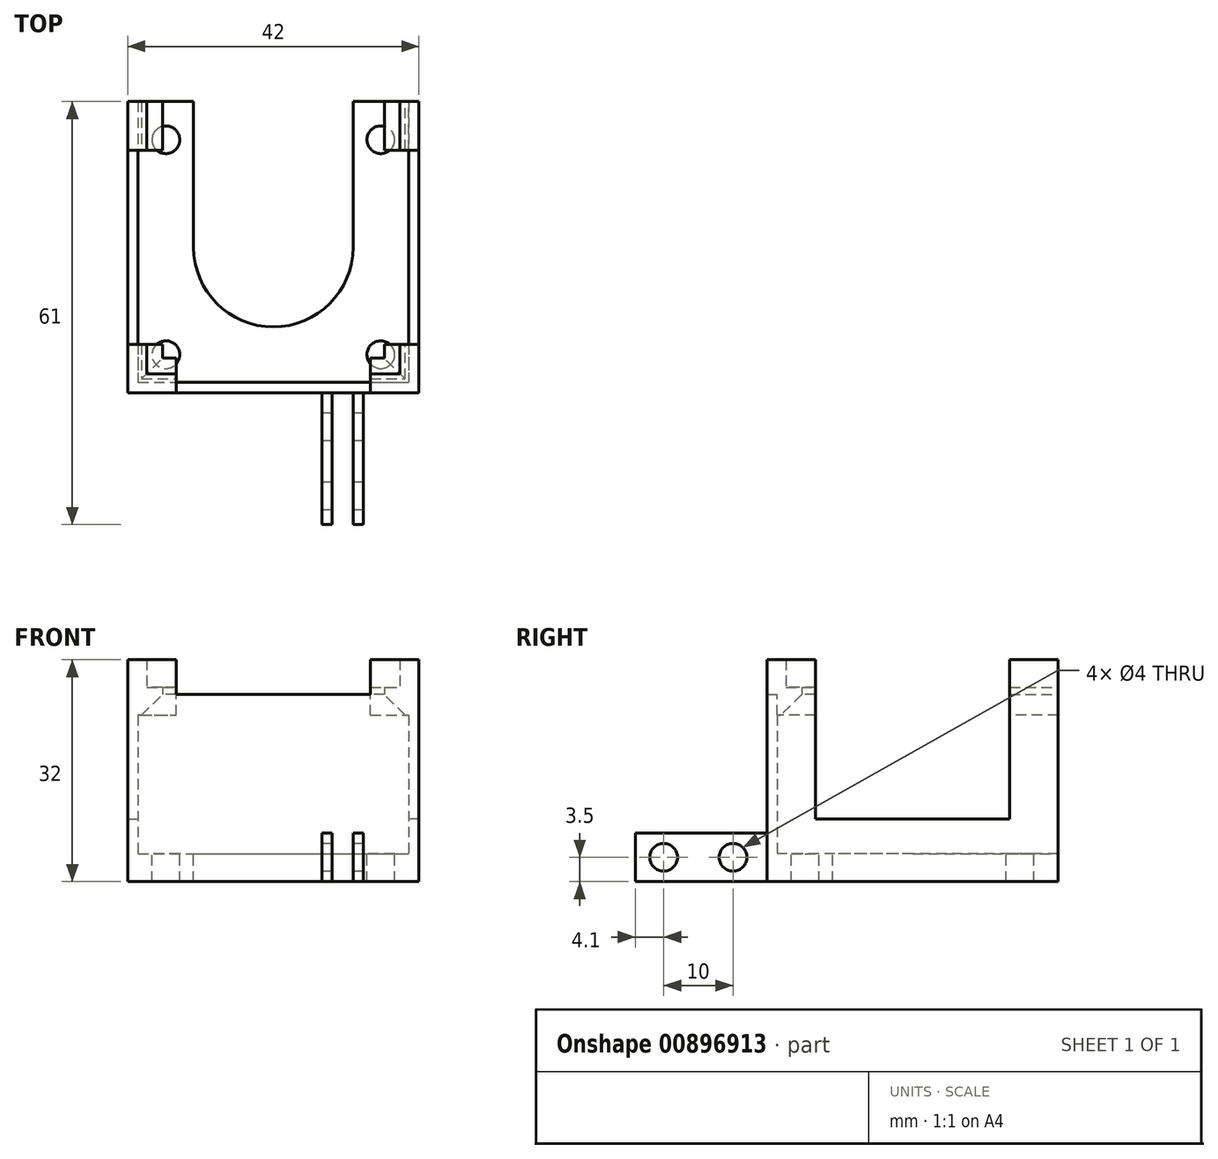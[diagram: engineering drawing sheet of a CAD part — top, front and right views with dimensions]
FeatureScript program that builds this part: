
annotation { "Feature Type Name" : "Feature", "Feature Type Description" : "" }
export const myFeature = defineFeature(function(context is Context, id is Id, definition is map)
    precondition{}
    {
        {
            var Q0;
            Q0=qCreatedBy(makeId("Top.planeOp"),FACE);
            var sketch = newSketch(context, id + "F0", { "sketchPlane" : qUnion([Q0])});
            skLineSegment(sketch, "E0.bottom", {"start": v(-19.5, 19.5) * mm, "end": v(19.5, 19.5) * mm});
            skLineSegment(sketch, "E0.top", {"start": v(-19.5, -19.5) * mm, "end": v(19.5, -19.5) * mm});
            skLineSegment(sketch, "E0.left", {"start": v(-19.5, 19.5) * mm, "end": v(-19.5, -19.5) * mm});
            skLineSegment(sketch, "E0.right", {"start": v(19.5, 19.5) * mm, "end": v(19.5, -19.5) * mm});
            skPoint(sketch, "E0.middle", {"position": v(0, 0) * mm});
            skLineSegment(sketch, "E1.0", {"start": v(21, 21) * mm, "end": v(21, -21) * mm});
            skLineSegment(sketch, "E1.1", {"start": v(-21, 21) * mm, "end": v(21, 21) * mm});
            skLineSegment(sketch, "E1.2", {"start": v(-21, 21) * mm, "end": v(-21, -21) * mm});
            skLineSegment(sketch, "E1.3", {"start": v(-21, -21) * mm, "end": v(21, -21) * mm});
            skLineSegment(sketch, "E2", {"start": v(21, 21) * mm, "end": v(21, 14) * mm});
            skLineSegment(sketch, "E3", {"start": v(21, 14) * mm, "end": v(19.5, 14) * mm});
            skLineSegment(sketch, "E4", {"start": v(-21, 14) * mm, "end": v(-19.5, 14) * mm});
            skLineSegment(sketch, "E5", {"start": v(-21, -14) * mm, "end": v(-19.5, -14) * mm});
            skLineSegment(sketch, "E6", {"start": v(-14, -19.5) * mm, "end": v(-14, -21) * mm});
            skLineSegment(sketch, "E7", {"start": v(14, -21) * mm, "end": v(14, -19.5) * mm});
            skLineSegment(sketch, "E8", {"start": v(21, -14) * mm, "end": v(19.5, -14) * mm});
            skLineSegment(sketch, "E9", {"start": v(-21, 14) * mm, "end": v(-21, 21) * mm});
            skCircle(sketch, "E10", {"center": v(0, 0) * mm, "radius": 11.5 * mm});
            skCircle(sketch, "E11", {"center": v(-15.5, 15.5) * mm, "radius": 2 * mm});
            skCircle(sketch, "E12", {"center": v(15.5, 15.5) * mm, "radius": 2 * mm});
            skCircle(sketch, "E13", {"center": v(15.5, -15.5) * mm, "radius": 2 * mm});
            skCircle(sketch, "E14", {"center": v(-15.5, -15.5) * mm, "radius": 2 * mm});
            skLineSegment(sketch, "E15", {"start": v(-19.5, 19.5) * mm, "end": v(-19.5, 21) * mm});
            skLineSegment(sketch, "E16", {"start": v(19.5, 19.5) * mm, "end": v(19.5, 21) * mm});
            skLineSegment(sketch, "E17", {"start": v(-21, -21) * mm, "end": v(-14, -21) * mm});
            skLineSegment(sketch, "E18", {"start": v(-11.5, 0) * mm, "end": v(-11.5, 21) * mm});
            skLineSegment(sketch, "E19", {"start": v(11.5, 0) * mm, "end": v(11.5, 21) * mm});
            skSolve(sketch);
        }
        {
            var Q0;
            Q0=makeQuery(id+"F0.imprint","IMPRINT",FACE,{"disambiguationData":[TD([[makeQuery(id+"F0.imprint","IMPRINT",EDGE,{"derivedFrom":sQuery(id+"F0.wireOp",EDGE,"E11")}),-1.0]])]});
            var Q1;
            {var subQ0=sQuery(id+"F0.wireOp",EDGE,"E4");Q1=makeQuery(id+"F0.imprint","IMPRINT",FACE,{"disambiguationData":[TD([[makeQuery(id+"F0.imprint","IMPRINT",EDGE,{"derivedFrom":subQ0}),-1.0]])]});}
            var Q2;
            {var subQ0=sQuery(id+"F0.wireOp",EDGE,"E3");Q2=makeQuery(id+"F0.imprint","IMPRINT",FACE,{"disambiguationData":[TD([[makeQuery(id+"F0.imprint","IMPRINT",EDGE,{"derivedFrom":subQ0}),-1.0]])]});}
            var Q3;
            {var subQ4=sQuery(id+"F0.wireOp",EDGE,"E7");Q3=makeQuery(id+"F0.imprint","IMPRINT",FACE,{"disambiguationData":[TD([[makeQuery(id+"F0.imprint","IMPRINT",EDGE,{"derivedFrom":subQ4}),-1.0]])]});}
            var Q4;
            {var subQ3=sQuery(id+"F0.wireOp",EDGE,"E5");Q4=makeQuery(id+"F0.imprint","IMPRINT",FACE,{"disambiguationData":[TD([[makeQuery(id+"F0.imprint","IMPRINT",EDGE,{"derivedFrom":subQ3}),-1.0]])]});}
            var Q5;
            {var subQ0=sQuery(id+"F0.wireOp",EDGE,"E4");Q5=makeQuery(id+"F0.imprint","IMPRINT",FACE,{"disambiguationData":[TD([[makeQuery(id+"F0.imprint","IMPRINT",EDGE,{"derivedFrom":subQ0}),1.0]])]});}
            var Q6;
            {var subQ0=sQuery(id+"F0.wireOp",EDGE,"E3");Q6=makeQuery(id+"F0.imprint","IMPRINT",FACE,{"disambiguationData":[TD([[makeQuery(id+"F0.imprint","IMPRINT",EDGE,{"derivedFrom":subQ0}),1.0]])]});}
            var Q7;
            {var subQ0=sQuery(id+"F0.wireOp",EDGE,"E6");Q7=makeQuery(id+"F0.imprint","IMPRINT",FACE,{"disambiguationData":[TD([[makeQuery(id+"F0.imprint","IMPRINT",EDGE,{"derivedFrom":subQ0}),1.0]])]});}
            var Q8;
            {var subQ3=sQuery(id+"F0.wireOp",EDGE,"E15");Q8=makeQuery(id+"F0.imprint","IMPRINT",FACE,{"disambiguationData":[TD([[makeQuery(id+"F0.imprint","IMPRINT",EDGE,{"derivedFrom":subQ3}),-1.0]])]});}
            var Q9;
            {var subQ0=sQuery(id+"F0.wireOp",EDGE,"E16");Q9=makeQuery(id+"F0.imprint","IMPRINT",FACE,{"disambiguationData":[TD([[makeQuery(id+"F0.imprint","IMPRINT",EDGE,{"derivedFrom":subQ0}),1.0]])]});}
            extrude(context, id + "F1", {"entities" : qUnion([Q0, Q1, Q2, Q3, Q4, Q5, Q6, Q7, Q8, Q9]), "oppositeDirection" : true, "depth" : 4 * mm, "offsetDistance" : 25 * mm});
        }
        {
            var Q0;
            {var subQ3=sQuery(id+"F0.wireOp",EDGE,"E5");Q0=makeQuery(id+"F0.imprint","IMPRINT",FACE,{"disambiguationData":[TD([[makeQuery(id+"F0.imprint","IMPRINT",EDGE,{"derivedFrom":subQ3}),-1.0]])]});}
            var Q1;
            {var subQ4=sQuery(id+"F0.wireOp",EDGE,"E7");Q1=makeQuery(id+"F0.imprint","IMPRINT",FACE,{"disambiguationData":[TD([[makeQuery(id+"F0.imprint","IMPRINT",EDGE,{"derivedFrom":subQ4}),-1.0]])]});}
            var Q2;
            Q2=makeQuery(id+"F0.imprint","IMPRINT",FACE,{"disambiguationData":[TD([[makeQuery(id+"F0.imprint","IMPRINT",EDGE,{"derivedFrom":sQuery(id+"F0.wireOp",EDGE,"wOJEcjxp-KVov-CLC1-gWga-9RxFXBWaR2St")}),-1.0]])]});
            var Q3;
            {var subQ0=sQuery(id+"F0.wireOp",EDGE,"y9VzjcNx-FhIy-98Bx-Yjvf-nXmHwvDM8nUN");Q3=makeQuery(id+"F0.imprint","IMPRINT",FACE,{"disambiguationData":[TD([[makeQuery(id+"F0.imprint","IMPRINT",EDGE,{"derivedFrom":subQ0}),1.0]])]});}
            var Q4;
            {var subQ0=sQuery(id+"F0.wireOp",EDGE,"E4");Q4=makeQuery(id+"F0.imprint","IMPRINT",FACE,{"disambiguationData":[TD([[makeQuery(id+"F0.imprint","IMPRINT",EDGE,{"derivedFrom":subQ0}),1.0]])]});}
            var Q5;
            {var subQ0=sQuery(id+"F0.wireOp",EDGE,"E3");Q5=makeQuery(id+"F0.imprint","IMPRINT",FACE,{"disambiguationData":[TD([[makeQuery(id+"F0.imprint","IMPRINT",EDGE,{"derivedFrom":subQ0}),-1.0]])]});}
            var Q6;
            {var subQ0=sQuery(id+"F0.wireOp",EDGE,"E6");Q6=makeQuery(id+"F0.imprint","IMPRINT",FACE,{"disambiguationData":[TD([[makeQuery(id+"F0.imprint","IMPRINT",EDGE,{"derivedFrom":subQ0}),1.0]])]});}
            extrude(context, id + "F2", {"entities" : qUnion([Q0, Q1, Q2, Q3, Q4, Q5, Q6]), "operationType" : NewBodyOperationType.ADD, "depth" : 23 * mm, "offsetDistance" : 25 * mm});
        }
        {
            var Q0;
            {var subQ0=sQuery(id+"F0.wireOp",EDGE,"E3");Q0=makeQuery(id+"F0.imprint","IMPRINT",FACE,{"disambiguationData":[TD([[makeQuery(id+"F0.imprint","IMPRINT",EDGE,{"derivedFrom":subQ0}),1.0]])]});}
            var Q1;
            {var subQ0=sQuery(id+"F0.wireOp",EDGE,"E4");Q1=makeQuery(id+"F0.imprint","IMPRINT",FACE,{"disambiguationData":[TD([[makeQuery(id+"F0.imprint","IMPRINT",EDGE,{"derivedFrom":subQ0}),-1.0]])]});}
            extrude(context, id + "F3", {"entities" : qUnion([Q0, Q1]), "operationType" : NewBodyOperationType.ADD, "depth" : 5 * mm, "offsetDistance" : 25 * mm});
        }
        {
            var Q0;
            Q0=makeQuery(id+"F2.opExtrude","CAP_FACE",FACE,{"disambiguationData":[OSD([sQuery(id+"F0.wireOp",EDGE,"E0.top"),sQuery(id+"F0.wireOp",EDGE,"E0.left"),sQuery(id+"F0.wireOp",EDGE,"E0.right"),sQuery(id+"F0.wireOp",EDGE,"E1.0"),sQuery(id+"F0.wireOp",EDGE,"E1.2"),sQuery(id+"F0.wireOp",EDGE,"E1.3"),sQuery(id+"F0.wireOp",EDGE,"E5"),sQuery(id+"F0.wireOp",EDGE,"E8")])],"isStart":false});
            var sketch = newSketch(context, id + "F4", { "sketchPlane" : qUnion([Q0])});
            skPoint(sketch, "E20", {"position": v(21, 21) * mm});
            skPoint(sketch, "E21", {"position": v(-21, 21) * mm});
            skPoint(sketch, "E22", {"position": v(21, -21) * mm});
            skPoint(sketch, "E23", {"position": v(-21, -21) * mm});
            skPoint(sketch, "E24", {"position": v(-21, 14) * mm});
            skPoint(sketch, "E25", {"position": v(21, 14) * mm});
            skPoint(sketch, "E26", {"position": v(21, -14) * mm});
            skPoint(sketch, "E27", {"position": v(14, -21) * mm});
            skPoint(sketch, "E28", {"position": v(-14, -21) * mm});
            skPoint(sketch, "E29", {"position": v(-21, -14) * mm});
            skLineSegment(sketch, "E30", {"start": v(-21, -14) * mm, "end": v(-21, -21) * mm});
            skLineSegment(sketch, "E31", {"start": v(-14, -21) * mm, "end": v(-21, -21) * mm});
            skLineSegment(sketch, "E32", {"start": v(14, -21) * mm, "end": v(21, -21) * mm});
            skLineSegment(sketch, "E33", {"start": v(21, -14) * mm, "end": v(21, -21) * mm});
            skLineSegment(sketch, "E34", {"start": v(21, 14) * mm, "end": v(21, 21) * mm});
            skLineSegment(sketch, "E35", {"start": v(-21, 14) * mm, "end": v(-21, 21) * mm});
            skLineSegment(sketch, "E36", {"start": v(-21, 14) * mm, "end": v(-16, 14) * mm});
            skLineSegment(sketch, "E37", {"start": v(-16, 14) * mm, "end": v(-16, 21) * mm});
            skLineSegment(sketch, "E38", {"start": v(-16, 21) * mm, "end": v(-21, 21) * mm});
            skLineSegment(sketch, "E39", {"start": v(21, 14) * mm, "end": v(16, 14) * mm});
            skLineSegment(sketch, "E40", {"start": v(16, 14) * mm, "end": v(16, 21) * mm});
            skLineSegment(sketch, "E41", {"start": v(16, 21) * mm, "end": v(21, 21) * mm});
            skLineSegment(sketch, "E42", {"start": v(14, -21) * mm, "end": v(14, -16) * mm});
            skLineSegment(sketch, "E43", {"start": v(14, -16) * mm, "end": v(16, -16) * mm});
            skLineSegment(sketch, "E44", {"start": v(16, -16) * mm, "end": v(16, -14) * mm});
            skLineSegment(sketch, "E45", {"start": v(16, -14) * mm, "end": v(21, -14) * mm});
            skLineSegment(sketch, "E46", {"start": v(-14, -21) * mm, "end": v(-14, -16) * mm});
            skLineSegment(sketch, "E47", {"start": v(-14, -16) * mm, "end": v(-16, -16) * mm});
            skLineSegment(sketch, "E48", {"start": v(-16, -16) * mm, "end": v(-16, -14) * mm});
            skLineSegment(sketch, "E49", {"start": v(-16, -14) * mm, "end": v(-21, -14) * mm});
            skLineSegment(sketch, "E50", {"start": v(-18.25, 21) * mm, "end": v(-18.25, 14) * mm});
            skLineSegment(sketch, "E51", {"start": v(-18.25, -14) * mm, "end": v(-18.25, -18.25) * mm});
            skLineSegment(sketch, "E52", {"start": v(-18.25, -18.25) * mm, "end": v(-14, -18.25) * mm});
            skLineSegment(sketch, "E53", {"start": v(14, -18.25) * mm, "end": v(18.25, -18.25) * mm});
            skLineSegment(sketch, "E54", {"start": v(18.25, -18.25) * mm, "end": v(18.25, -14) * mm});
            skLineSegment(sketch, "E55", {"start": v(18.25, 14) * mm, "end": v(18.25, 21) * mm});
            skLineSegment(sketch, "E56", {"start": v(18.25, 21) * mm, "end": v(21, 21) * mm});
            skLineSegment(sketch, "E57", {"start": v(-18.25, 21) * mm, "end": v(-21, 21) * mm});
            skLineSegment(sketch, "E58", {"start": v(-18.25, -14) * mm, "end": v(-21, -14) * mm});
            skLineSegment(sketch, "E59", {"start": v(-14, -18.25) * mm, "end": v(-14, -21) * mm});
            skLineSegment(sketch, "E60", {"start": v(14, -18.25) * mm, "end": v(14, -21) * mm});
            skLineSegment(sketch, "E61", {"start": v(18.25, -14) * mm, "end": v(21, -14) * mm});
            skLineSegment(sketch, "E62", {"start": v(18.25, 14) * mm, "end": v(21, 14) * mm});
            skLineSegment(sketch, "E63", {"start": v(-21, -21) * mm, "end": v(-16, -16) * mm});
            skSolve(sketch);
        }
        {
            var Q0;
            {var subQ0=sQuery(id+"F4.wireOp",EDGE,"E34");Q0=makeQuery(id+"F4.imprint","IMPRINT",FACE,{"disambiguationData":[TD([[makeQuery(id+"F4.imprint","IMPRINT",EDGE,{"derivedFrom":subQ0}),1.0]])]});}
            var Q1;
            {var subQ1=sQuery(id+"F4.wireOp",EDGE,"E32");Q1=makeQuery(id+"F4.imprint","IMPRINT",FACE,{"disambiguationData":[TD([[makeQuery(id+"F4.imprint","IMPRINT",EDGE,{"derivedFrom":subQ1}),1.0]])]});}
            var Q2;
            {var subQ0=sQuery(id+"F4.wireOp",EDGE,"E31");Q2=makeQuery(id+"F4.imprint","IMPRINT",FACE,{"disambiguationData":[TD([[makeQuery(id+"F4.imprint","IMPRINT",EDGE,{"derivedFrom":subQ0}),1.0]])]});}
            var Q3;
            {var subQ0=sQuery(id+"F4.wireOp",EDGE,"E52");Q3=makeQuery(id+"F4.imprint","IMPRINT",FACE,{"disambiguationData":[TD([[makeQuery(id+"F4.imprint","IMPRINT",EDGE,{"derivedFrom":subQ0}),-1.0]])]});}
            var Q4;
            {var subQ2=sQuery(id+"F4.wireOp",EDGE,"E51");Q4=makeQuery(id+"F4.imprint","IMPRINT",FACE,{"disambiguationData":[TD([[makeQuery(id+"F4.imprint","IMPRINT",EDGE,{"derivedFrom":subQ2}),-1.0]])]});}
            var Q5;
            {var subQ0=sQuery(id+"F4.wireOp",EDGE,"E30");Q5=makeQuery(id+"F4.imprint","IMPRINT",FACE,{"disambiguationData":[TD([[makeQuery(id+"F4.imprint","IMPRINT",EDGE,{"derivedFrom":subQ0}),1.0]])]});}
            var Q6;
            {var subQ0=sQuery(id+"F4.wireOp",EDGE,"E35");Q6=makeQuery(id+"F4.imprint","IMPRINT",FACE,{"disambiguationData":[TD([[makeQuery(id+"F4.imprint","IMPRINT",EDGE,{"derivedFrom":subQ0}),-1.0]])]});}
            var Q7;
            {var subQ0=sQuery(id+"F4.wireOp",EDGE,"E53");Q7=makeQuery(id+"F4.imprint","IMPRINT",FACE,{"disambiguationData":[TD([[makeQuery(id+"F4.imprint","IMPRINT",EDGE,{"derivedFrom":subQ0}),-1.0]])]});}
            extrude(context, id + "F5", {"entities" : qUnion([Q0, Q1, Q2, Q3, Q4, Q5, Q6, Q7]), "operationType" : NewBodyOperationType.ADD, "depth" : 5 * mm, "offsetDistance" : 25 * mm});
        }
        {
            var Q0;
            {var subQ0=sQuery(id+"F4.wireOp",EDGE,"E40");Q0=makeQuery(id+"F4.imprint","IMPRINT",FACE,{"disambiguationData":[TD([[makeQuery(id+"F4.imprint","IMPRINT",EDGE,{"derivedFrom":subQ0}),-1.0]])]});}
            var Q1;
            {var subQ1=sQuery(id+"F4.wireOp",EDGE,"E43");Q1=makeQuery(id+"F4.imprint","IMPRINT",FACE,{"disambiguationData":[TD([[makeQuery(id+"F4.imprint","IMPRINT",EDGE,{"derivedFrom":subQ1}),-1.0]])]});}
            var Q2;
            {var subQ2=sQuery(id+"F4.wireOp",EDGE,"E47");Q2=makeQuery(id+"F4.imprint","IMPRINT",FACE,{"disambiguationData":[TD([[makeQuery(id+"F4.imprint","IMPRINT",EDGE,{"derivedFrom":subQ2}),1.0]])]});}
            var Q3;
            {var subQ0=sQuery(id+"F4.wireOp",EDGE,"E48");Q3=makeQuery(id+"F4.imprint","IMPRINT",FACE,{"disambiguationData":[TD([[makeQuery(id+"F4.imprint","IMPRINT",EDGE,{"derivedFrom":subQ0}),1.0]])]});}
            var Q4;
            {var subQ0=sQuery(id+"F4.wireOp",EDGE,"E37");Q4=makeQuery(id+"F4.imprint","IMPRINT",FACE,{"disambiguationData":[TD([[makeQuery(id+"F4.imprint","IMPRINT",EDGE,{"derivedFrom":subQ0}),1.0]])]});}
            extrude(context, id + "F6", {"entities" : qUnion([Q0, Q1, Q2, Q3, Q4]), "operationType" : NewBodyOperationType.ADD, "depth" : 1 * mm, "offsetDistance" : 25 * mm});
        }
        {
            var Q0;
            {var subQ0=sQuery(id+"F4.wireOp",EDGE,"E55");var subQ1=sQuery(id+"F4.wireOp",EDGE,"E41");var subQ2=sQuery(id+"F4.wireOp",EDGE,"E39");Q0=makeQuery(id+"F6.boolean.opBoolean","MERGE",FACE,{"derivedFrom":[makeQuery(id+"F5.opExtrude","CAP_FACE",FACE,{"disambiguationData":[OSD([sQuery(id+"F4.wireOp",EDGE,"E34"),subQ2,subQ1,subQ0])],"isStart":true}),makeQuery(id+"F6.opExtrude","CAP_FACE",FACE,{"disambiguationData":[OSD([subQ2,sQuery(id+"F4.wireOp",EDGE,"E40"),subQ1,subQ0])],"isStart":true})]});}
            var Q1;
            {var subQ0=sQuery(id+"F4.wireOp",EDGE,"E54");var subQ1=sQuery(id+"F4.wireOp",EDGE,"E53");var subQ2=sQuery(id+"F4.wireOp",EDGE,"E45");var subQ3=sQuery(id+"F4.wireOp",EDGE,"E42");Q1=makeQuery(id+"F6.boolean.opBoolean","MERGE",FACE,{"derivedFrom":[makeQuery(id+"F5.opExtrude","CAP_FACE",FACE,{"disambiguationData":[OSD([sQuery(id+"F4.wireOp",EDGE,"E32"),sQuery(id+"F4.wireOp",EDGE,"E33"),subQ3,subQ2,subQ1,subQ0])],"isStart":true}),makeQuery(id+"F6.opExtrude","CAP_FACE",FACE,{"disambiguationData":[OSD([subQ3,sQuery(id+"F4.wireOp",EDGE,"E43"),sQuery(id+"F4.wireOp",EDGE,"E44"),subQ2,subQ1,subQ0])],"isStart":true})]});}
            var Q2;
            {var subQ0=sQuery(id+"F4.wireOp",EDGE,"E52");var subQ1=sQuery(id+"F4.wireOp",EDGE,"E51");var subQ2=sQuery(id+"F4.wireOp",EDGE,"E49");var subQ3=sQuery(id+"F4.wireOp",EDGE,"E46");Q2=makeQuery(id+"F6.boolean.opBoolean","MERGE",FACE,{"derivedFrom":[makeQuery(id+"F5.opExtrude","CAP_FACE",FACE,{"disambiguationData":[OSD([sQuery(id+"F4.wireOp",EDGE,"E30"),sQuery(id+"F4.wireOp",EDGE,"E31"),subQ3,subQ2,subQ1,subQ0])],"isStart":true}),makeQuery(id+"F6.opExtrude","CAP_FACE",FACE,{"disambiguationData":[OSD([subQ3,sQuery(id+"F4.wireOp",EDGE,"E47"),sQuery(id+"F4.wireOp",EDGE,"E48"),subQ2,subQ1,subQ0])],"isStart":true})]});}
            var Q3;
            {var subQ0=sQuery(id+"F4.wireOp",EDGE,"E50");var subQ1=sQuery(id+"F4.wireOp",EDGE,"E38");var subQ2=sQuery(id+"F4.wireOp",EDGE,"E36");Q3=makeQuery(id+"F6.boolean.opBoolean","MERGE",FACE,{"derivedFrom":[makeQuery(id+"F5.opExtrude","CAP_FACE",FACE,{"disambiguationData":[OSD([sQuery(id+"F4.wireOp",EDGE,"E35"),subQ2,subQ1,subQ0])],"isStart":true}),makeQuery(id+"F6.opExtrude","CAP_FACE",FACE,{"disambiguationData":[OSD([subQ2,sQuery(id+"F4.wireOp",EDGE,"E37"),subQ1,subQ0])],"isStart":true})]});}
            extrude(context, id + "F7", {"entities" : qUnion([Q0, Q1, Q2, Q3]), "operationType" : NewBodyOperationType.ADD, "depth" : 3 * mm, "offsetDistance" : 25 * mm});
        }
        {
            var Q0;
            Q0=makeQuery(id+"F7.opExtrude","CAP_EDGE",EDGE,{"disambiguationData":[OSD([sQuery(id+"F4.wireOp",EDGE,"E40")])],"isStart":false});
            var Q1;
            Q1=makeQuery(id+"F7.opExtrude","CAP_EDGE",EDGE,{"disambiguationData":[OSD([sQuery(id+"F4.wireOp",EDGE,"E43")])],"isStart":false});
            var Q2;
            Q2=makeQuery(id+"F7.opExtrude","CAP_EDGE",EDGE,{"disambiguationData":[OSD([sQuery(id+"F4.wireOp",EDGE,"E44")])],"isStart":false});
            var Q3;
            Q3=makeQuery(id+"F7.opExtrude","CAP_EDGE",EDGE,{"disambiguationData":[OSD([sQuery(id+"F4.wireOp",EDGE,"E47")])],"isStart":false});
            var Q4;
            Q4=makeQuery(id+"F7.opExtrude","CAP_EDGE",EDGE,{"disambiguationData":[OSD([sQuery(id+"F4.wireOp",EDGE,"E48")])],"isStart":false});
            var Q5;
            Q5=makeQuery(id+"F7.opExtrude","CAP_EDGE",EDGE,{"disambiguationData":[OSD([sQuery(id+"F4.wireOp",EDGE,"E37")])],"isStart":false});
            chamfer(context, id + "F8", {"entities" : qUnion([Q0, Q1, Q2, Q3, Q4, Q5]), "width" : 3 * mm, "tangentPropagation" : true});
        }
        {
            var Q0;
            {var subQ0=sQuery(id+"F0.wireOp",EDGE,"E1.3");Q0=makeQuery(id+"F5.boolean.opBoolean","MERGE",FACE,{"derivedFrom":[makeQuery(id+"F2.boolean.opBoolean","MERGE",FACE,{"derivedFrom":[makeQuery(id+"F1.opExtrude","SWEPT_FACE",FACE,{"disambiguationData":[OSD([subQ0])]}),makeQuery(id+"F2.opExtrude","SWEPT_FACE",FACE,{"disambiguationData":[OSD([subQ0])]})]}),makeQuery(id+"F5.opExtrude","SWEPT_FACE",FACE,{"disambiguationData":[OSD([sQuery(id+"F4.wireOp",EDGE,"E31")])]}),makeQuery(id+"F5.opExtrude","SWEPT_FACE",FACE,{"disambiguationData":[OSD([sQuery(id+"F4.wireOp",EDGE,"E32")])]})]});}
            var sketch = newSketch(context, id + "F9", { "sketchPlane" : qUnion([Q0])});
            skLineSegment(sketch, "E64.bottom", {"start": v(7, -4) * mm, "end": v(8.5, -4) * mm});
            skLineSegment(sketch, "E64.top", {"start": v(7, 3) * mm, "end": v(8.5, 3) * mm});
            skLineSegment(sketch, "E64.left", {"start": v(7, -4) * mm, "end": v(7, 3) * mm});
            skLineSegment(sketch, "E64.right", {"start": v(8.5, -4) * mm, "end": v(8.5, 3) * mm});
            skLineSegment(sketch, "E65.bottom", {"start": v(11.5, -4) * mm, "end": v(13, -4) * mm});
            skLineSegment(sketch, "E65.top", {"start": v(11.5, 3) * mm, "end": v(13, 3) * mm});
            skLineSegment(sketch, "E65.left", {"start": v(11.5, -4) * mm, "end": v(11.5, 3) * mm});
            skLineSegment(sketch, "E65.right", {"start": v(13, -4) * mm, "end": v(13, 3) * mm});
            skSolve(sketch);
        }
        {
            var Q0;
            Q0=makeQuery(id+"F9.imprint","IMPRINT",FACE,{"disambiguationData":[TD([[makeQuery(id+"F9.imprint","IMPRINT",EDGE,{"derivedFrom":sQuery(id+"F9.wireOp",EDGE,"E64.bottom")}),1.0]])]});
            var Q1;
            Q1=makeQuery(id+"F9.imprint","IMPRINT",FACE,{"disambiguationData":[TD([[makeQuery(id+"F9.imprint","IMPRINT",EDGE,{"derivedFrom":sQuery(id+"F9.wireOp",EDGE,"E65.bottom")}),1.0]])]});
            extrude(context, id + "F10", {"entities" : qUnion([Q0, Q1]), "operationType" : NewBodyOperationType.ADD, "depth" : 19 * mm, "offsetDistance" : 25 * mm});
        }
        {
            var Q0;
            Q0=makeQuery(id+"F10.opExtrude","SWEPT_FACE",FACE,{"disambiguationData":[OSD([sQuery(id+"F9.wireOp",EDGE,"E64.left")])]});
            var sketch = newSketch(context, id + "F11", { "sketchPlane" : qUnion([Q0])});
            skCircle(sketch, "E66", {"center": v(25.9, -0.5) * mm, "radius": 2 * mm});
            skCircle(sketch, "E67", {"center": v(35.9, -0.5) * mm, "radius": 2 * mm});
            skSolve(sketch);
        }
        {
            var Q0;
            Q0=makeQuery(id+"F11.imprint","IMPRINT",FACE,{"disambiguationData":[TD([[makeQuery(id+"F11.imprint","IMPRINT",EDGE,{"derivedFrom":sQuery(id+"F11.wireOp",EDGE,"E66")}),1.0]])]});
            var Q1;
            Q1=makeQuery(id+"F11.imprint","IMPRINT",FACE,{"disambiguationData":[TD([[makeQuery(id+"F11.imprint","IMPRINT",EDGE,{"derivedFrom":sQuery(id+"F11.wireOp",EDGE,"E67")}),1.0]])]});
            extrude(context, id + "F12", {"entities" : qUnion([Q0, Q1]), "operationType" : NewBodyOperationType.REMOVE, "endBound" : BoundingType.THROUGH_ALL, "oppositeDirection" : true, "depth" : 25 * mm, "offsetDistance" : 25 * mm});
        }
    });
